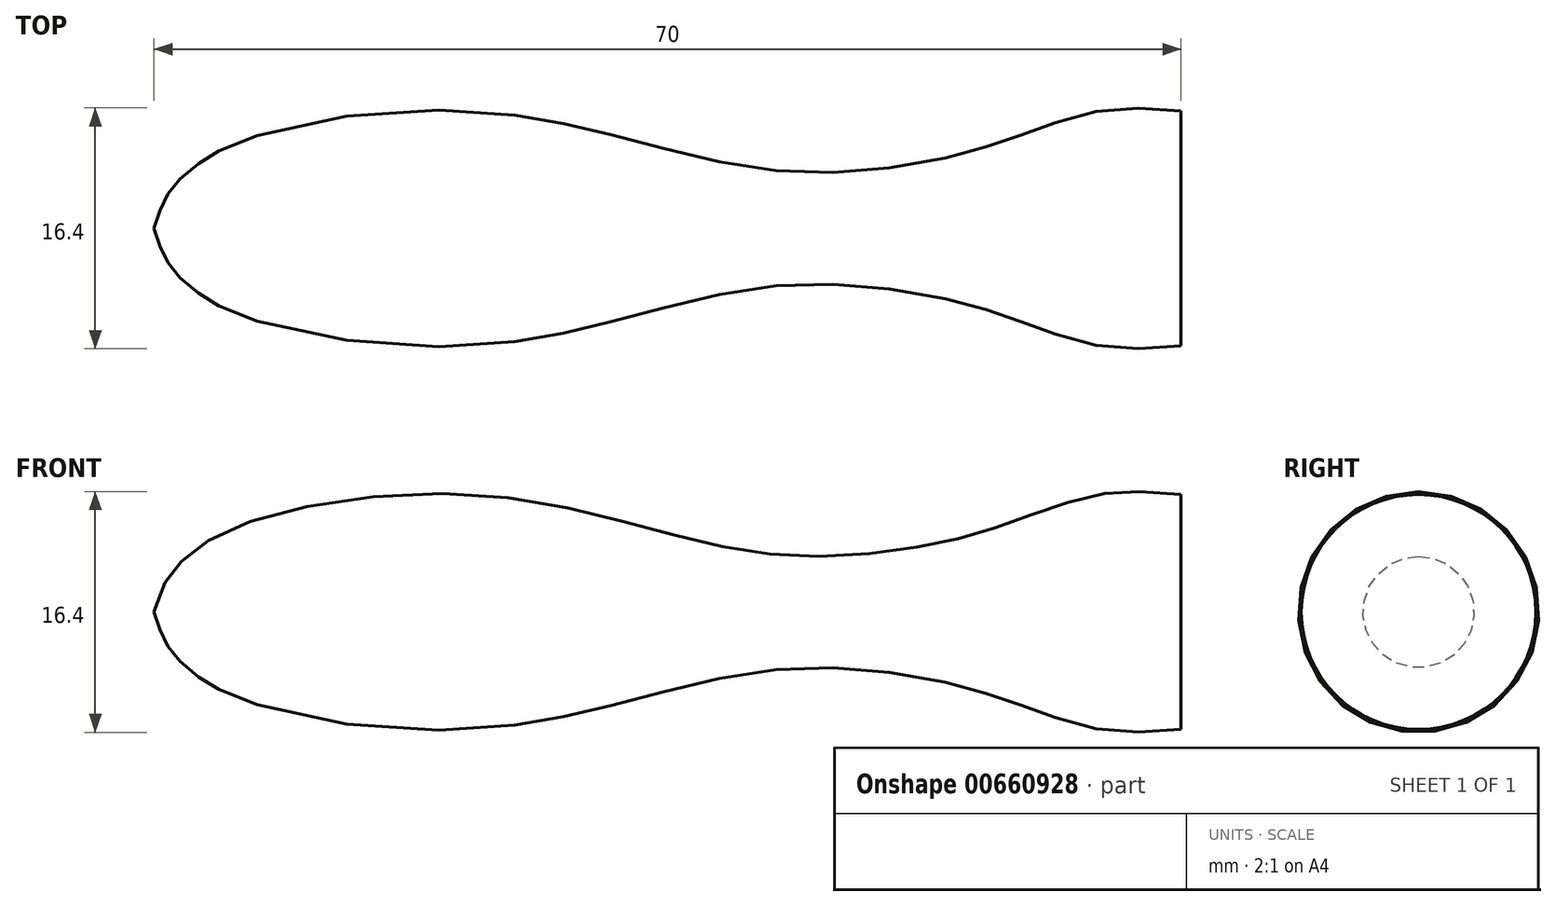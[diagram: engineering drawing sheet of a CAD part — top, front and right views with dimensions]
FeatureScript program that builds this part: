
annotation { "Feature Type Name" : "Feature", "Feature Type Description" : "" }
export const myFeature = defineFeature(function(context is Context, id is Id, definition is map)
    precondition{}
    {
        {
            var Q0;
            Q0=qCreatedBy(makeId("Front.planeOp"),FACE);
            var sketch = newSketch(context, id + "F0", { "sketchPlane" : qUnion([Q0])});
            skLineSegment(sketch, "E0", {"start": v(0, 0) * mm, "end": v(70, 0) * mm, "construction": true});
            skLineSegment(sketch, "E1", {"start": v(70, 0) * mm, "end": v(70, 8) * mm});
            skFitSpline(sketch, "E2", {"points": [v(70, 8) * mm, v(64.37, 8) * mm, v(58.77, 6.24) * mm, v(53.1, 4.62) * mm, v(43.97, 3.81) * mm, v(34.72, 5.43) * mm, v(21.65, 8) * mm, v(5.8, 5.9) * mm, v(1.41, 2.96) * mm, v(0, 0) * mm], "startDerivative": vector(-74.38, 6.47) * mm, "endDerivative": vector(-18.06, -61.65) * mm});
            skSolve(sketch);
        }
        {
            var Q0;
            Q0=sQuery(id+"F0.wireOp",EDGE,"E1");
            var Q1;
            Q1=sQuery(id+"F0.wireOp",EDGE,"E2");
            var Q2;
            Q2=sQuery(id+"F0.wireOp",EDGE,"E0");
            revolve(context, id + "F1", {"bodyType" : ToolBodyType.SURFACE, "surfaceEntities" : qUnion([Q0, Q1]), "axis" : qUnion([Q2]), "revolveType" : RevolveType.FULL});
        }
    });
